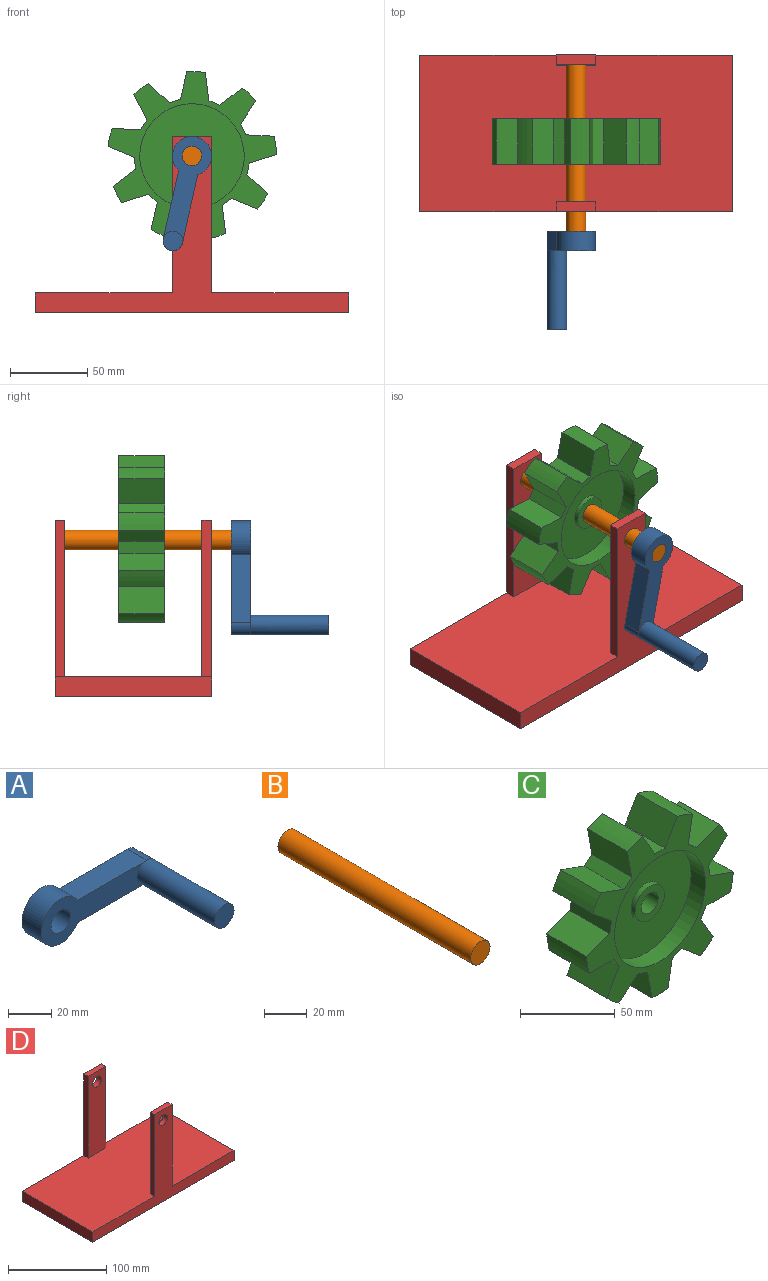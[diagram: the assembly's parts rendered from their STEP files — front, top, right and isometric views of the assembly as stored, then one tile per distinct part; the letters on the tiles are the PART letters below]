
ASSEMBLY  parts=4 mates=3
PART A: 10 faces, bbox 75.6x63.5x25.4 mm
  f0: plane 45.54x12.7mm, normal (0,0,1), area 578.3mm2, adj f1,f4,f5,f6,f9
  f1: cylinder r=12.7mm len=25.4mm, axis (0,-1,0), area 844.5mm2, adj f0,f2,f5,f6
  f2: plane 45.54x12.7mm, normal (0,0,-1), area 578.3mm2, adj f1,f4,f5,f6
  f3: cylinder r=6.35mm len=12.7mm, axis (0,-1,0), area 506.7mm2, adj f5,f6
  f4: cylinder r=6.35mm len=12.7mm, axis (0,-1,0), area 253.4mm2, adj f0,f2,f5,f6,f9
  f5: plane 75.59x25.4mm, normal (0,1,0), area 1007.1mm2, adj f0,f1,f2,f3,f4
  f6: plane 75.59x25.4mm, normal (0,-1,0), area 881.2mm2, adj f0,f1,f2,f3,f4,f7
  f7: cylinder r=6.35mm len=50.8mm, axis (0,1,0), area 2026.8mm2, adj f6,f8,f9
  f8: plane 12.7x12.7mm, normal (0,-1,0), area 126.7mm2, adj f7
  f9: plane 7.53x6.41mm, normal (0,1,0), area 0.8mm2, adj f0,f4,f7
PART B: 3 faces, bbox 12.7x127x12.7 mm
  f0: cylinder r=6.35mm len=127mm, axis (0,1,0), area 5067.1mm2, adj f1,f2
  f1: plane 12.7x12.7mm, normal (0,1,0), area 126.7mm2, adj f0
  f2: plane 12.7x12.7mm, normal (0,-1,0), area 126.7mm2, adj f0
PART C: 47 faces, bbox 109.4x29.8x108.1 mm
  f0: cylinder r=54.84mm len=29.78mm, axis (0,1,0), area 358.5mm2, adj f2,f32,f34,f46
  f1: plane 29.78x5.84mm, normal (-0.64,0,0.77), area 226.9mm2, adj f2,f3,f32,f34
  f2: plane 29.78x18.1mm, normal (-0.98,0,-0.17), area 547.3mm2, adj f0,f1,f32,f34
  f3: plane 29.78x17.27mm, normal (0.34,0,0.94), area 547.3mm2, adj f1,f4,f32,f34
  f4: cylinder r=54.84mm len=29.78mm, axis (0,1,0), area 358.5mm2, adj f3,f6,f32,f34
  f5: plane 29.78x7.5mm, normal (-0.98,0,0.17), area 226.9mm2, adj f6,f7,f32,f34
  f6: plane 29.78x14.08mm, normal (-0.64,0,-0.77), area 547.3mm2, adj f4,f5,f32,f34
  f7: plane 29.78x17.27mm, normal (-0.34,0,0.94), area 547.3mm2, adj f5,f8,f32,f34
  f8: cylinder r=54.84mm len=29.78mm, axis (0,1,0), area 358.5mm2, adj f7,f10,f32,f34
  f9: plane 29.78x6.6mm, normal (-0.87,0,-0.5), area 226.9mm2, adj f10,f11,f32,f34
  f10: plane 29.78x18.38mm, normal (0,0,-1), area 547.3mm2, adj f8,f9,f32,f34
  f11: plane 29.78x15.91mm, normal (-0.87,0,0.5), area 547.3mm2, adj f9,f12,f32,f34
  f12: cylinder r=54.84mm len=29.78mm, axis (0,1,0), area 358.5mm2, adj f11,f14,f32,f34
  f13: plane 29.78x7.16mm, normal (-0.34,0,-0.94), area 226.9mm2, adj f14,f15,f32,f34
  f14: plane 29.78x14.08mm, normal (0.64,0,-0.77), area 547.3mm2, adj f12,f13,f32,f34
  f15: plane 29.78x18.1mm, normal (-0.98,0,-0.17), area 547.3mm2, adj f13,f16,f32,f34
  f16: cylinder r=54.84mm len=29.78mm, axis (0,1,0), area 358.5mm2, adj f15,f18,f32,f34
  f17: plane 29.78x7.16mm, normal (0.34,0,-0.94), area 226.9mm2, adj f18,f19,f32,f34
  f18: plane 29.78x18.1mm, normal (0.98,0,-0.17), area 547.3mm2, adj f16,f17,f32,f34
  f19: plane 29.78x14.08mm, normal (-0.64,0,-0.77), area 547.3mm2, adj f17,f20,f32,f34
  f20: cylinder r=54.84mm len=29.78mm, axis (0,1,0), area 358.5mm2, adj f19,f22,f32,f34
  f21: plane 29.78x6.6mm, normal (0.87,0,-0.5), area 226.9mm2, adj f22,f23,f32,f34
  f22: plane 29.78x15.91mm, normal (0.87,0,0.5), area 547.3mm2, adj f20,f21,f32,f34
  f23: plane 29.78x18.38mm, normal (0,0,-1), area 547.3mm2, adj f21,f24,f32,f34
  f24: cylinder r=54.84mm len=29.78mm, axis (0,1,0), area 358.5mm2, adj f23,f26,f32,f34
  f25: plane 29.78x7.5mm, normal (0.98,0,0.17), area 226.9mm2, adj f26,f27,f32,f34
  f26: plane 29.78x17.27mm, normal (0.34,0,0.94), area 547.3mm2, adj f24,f25,f32,f34
  f27: plane 29.78x14.08mm, normal (0.64,0,-0.77), area 547.3mm2, adj f25,f28,f32,f34
  f28: cylinder r=54.84mm len=29.78mm, axis (0,1,0), area 358.5mm2, adj f27,f30,f32,f34
  f29: plane 29.78x5.84mm, normal (0.64,0,0.77), area 226.9mm2, adj f30,f31,f32,f34
  f30: plane 29.78x17.27mm, normal (-0.34,0,0.94), area 547.3mm2, adj f28,f29,f32,f34
  f31: plane 29.78x18.1mm, normal (0.98,0,-0.17), area 547.3mm2, adj f29,f32,f33,f34
  f32: plane 109.44x108.11mm, normal (0,1,0), area 3185mm2, adj f0,f1,f2,f3,f4,f5,f6,f7
  f33: cylinder r=54.84mm len=29.78mm, axis (0,1,0), area 358.5mm2, adj f31,f32,f34,f45
  f34: plane 109.44x108.11mm, normal (0,-1,0), area 3185mm2, adj f0,f1,f2,f3,f4,f5,f6,f7
  f35: cylinder r=33.9mm len=67.8mm, axis (0,1,0), area 2271.9mm2, adj f34,f36
  f36: plane 67.8x67.8mm, normal (0,-1,0), area 3233.7mm2, adj f35,f37
  f37: cylinder r=10.95mm len=21.89mm, axis (0,1,0), area 210.9mm2, adj f36,f38
  f38: plane 21.89x21.89mm, normal (0,-1,0), area 248.6mm2, adj f37,f39
  f39: cylinder r=6.38mm len=14.58mm, axis (0,1,0), area 584.4mm2, adj f38,f40
  f40: plane 21.89x21.89mm, normal (0,1,0), area 248.6mm2, adj f39,f41
  f41: cylinder r=10.95mm len=21.89mm, axis (0,1,0), area 210.9mm2, adj f40,f42
  f42: plane 67.8x67.8mm, normal (0,1,0), area 3233.7mm2, adj f41,f43
  f43: cylinder r=33.9mm len=67.8mm, axis (0,1,0), area 2271.9mm2, adj f32,f42
  f44: plane 29.78x7.62mm, normal (0,0,1), area 226.9mm2, adj f32,f34,f45,f46
  f45: plane 29.78x15.91mm, normal (-0.87,0,0.5), area 547.3mm2, adj f32,f33,f34,f44
  f46: plane 29.78x15.91mm, normal (0.87,0,0.5), area 547.3mm2, adj f0,f32,f34,f44
PART D: 16 faces, bbox 203.2x101.6x114.3 mm
  f0: plane 203.2x101.6mm, normal (0,0,1), area 20322.5mm2, adj f1,f3,f4,f5,f6,f7,f8,f10
  f1: plane 101.6x12.7mm, normal (-1,0,0), area 1290.3mm2, adj f0,f2,f4,f5
  f2: plane 203.2x101.6mm, normal (0,0,-1), area 20645.1mm2, adj f1,f3,f4,f5
  f3: plane 101.6x12.7mm, normal (1,0,0), area 1290.3mm2, adj f0,f2,f4,f5
  f4: plane 203.2x114.3mm, normal (0,-1,0), area 5034.6mm2, adj f0,f1,f2,f3,f10,f11,f13,f14
  f5: plane 203.2x114.3mm, normal (0,1,0), area 5034.6mm2, adj f0,f1,f2,f3,f6,f8,f9,f15
  f6: plane 101.6x6.35mm, normal (-1,0,0), area 645.2mm2, adj f0,f5,f7,f9
  f7: plane 101.6x25.4mm, normal (0,-1,0), area 2454mm2, adj f0,f6,f8,f9,f15
  f8: plane 101.6x6.35mm, normal (1,0,0), area 645.2mm2, adj f0,f5,f7,f9
  f9: plane 25.4x6.35mm, normal (0,0,1), area 161.3mm2, adj f5,f6,f7,f8
  f10: plane 101.6x6.35mm, normal (-1,0,0), area 645.2mm2, adj f0,f4,f12,f13
  f11: plane 101.6x6.35mm, normal (1,0,0), area 645.2mm2, adj f0,f4,f12,f13
  f12: plane 101.6x25.4mm, normal (0,1,0), area 2454mm2, adj f0,f10,f11,f13,f14
  f13: plane 25.4x6.35mm, normal (0,0,1), area 161.3mm2, adj f4,f10,f11,f12
  f14: cylinder r=6.35mm len=12.7mm, axis (0,1,0), area 253.4mm2, adj f4,f12
  f15: cylinder r=6.35mm len=12.7mm, axis (0,1,0), area 253.4mm2, adj f5,f7
PLACE A rot(axis=(0,1,0),102.7deg) t=(-203.15,43.04,120.32)mm
PLACE B rot(axis=(0,1,0),102.7deg) t=(-203.15,43.04,120.32)mm
PLACE C rot(axis=(0,1,0),102.7deg) t=(-203.15,43.98,120.32)mm
PLACE D t=(-145.44,49.39,48.11)mm
MATE fastened A.f1 <-> B.f0  axis (0,-1,0) through (-145.44,-26.81,107.27)mm
MATE fastened B.f0 <-> C.f0  axis (0,1,0) through (-145.44,36.69,107.27)mm
MATE revolute D.f14 <-> B.f0  axis (0,1,0) through (-145.44,100.19,107.27)mm
